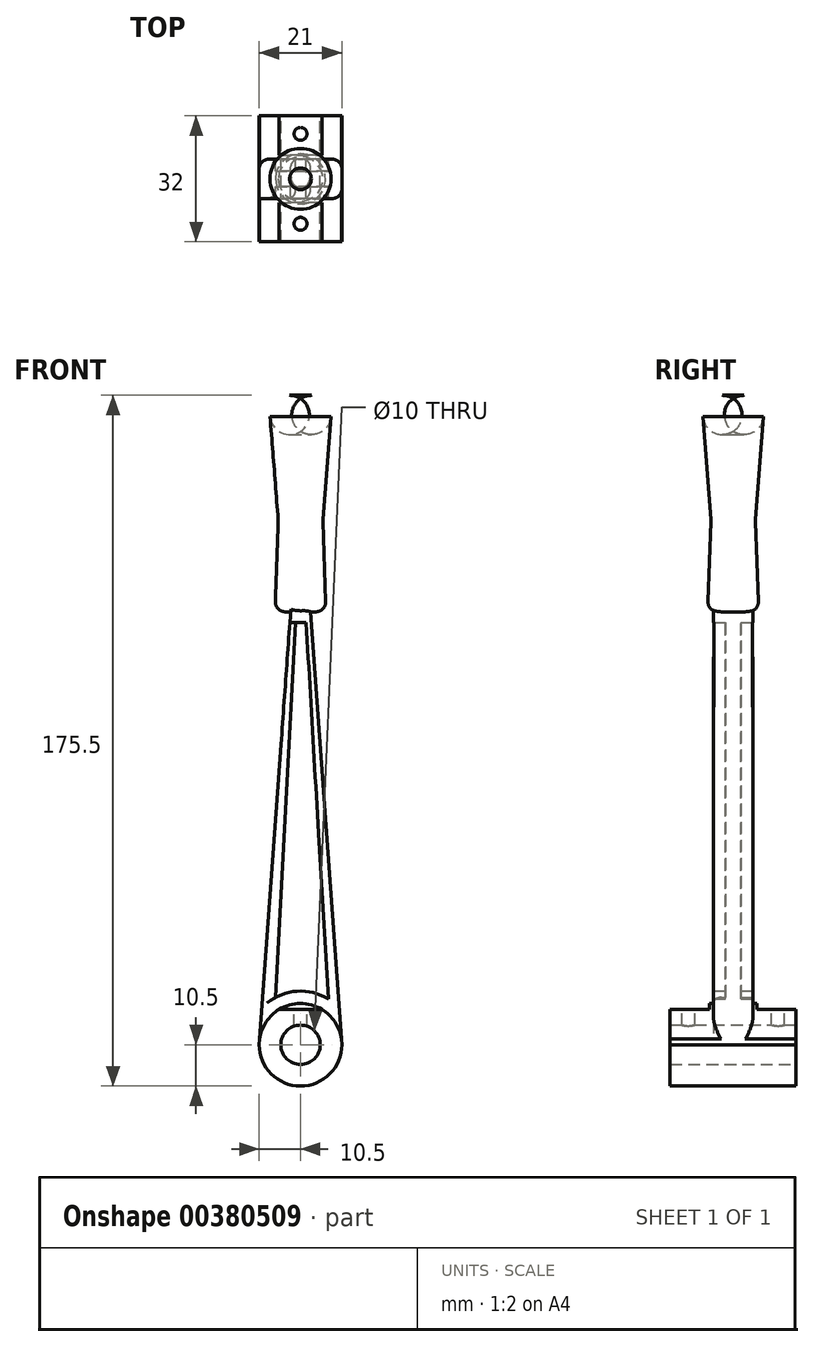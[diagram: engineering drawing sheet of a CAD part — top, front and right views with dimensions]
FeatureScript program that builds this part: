
annotation { "Feature Type Name" : "Feature", "Feature Type Description" : "" }
export const myFeature = defineFeature(function(context is Context, id is Id, definition is map)
    precondition{}
    {
        {
            var Q0;
            Q0=qCreatedBy(makeId("Front.planeOp"),FACE);
            var sketch = newSketch(context, id + "F0", { "sketchPlane" : qUnion([Q0])});
            skCircle(sketch, "E0", {"center": v(0, 0) * mm, "radius": 10.5 * mm});
            skCircle(sketch, "E1", {"center": v(0, 0) * mm, "radius": 5 * mm});
            skLineSegment(sketch, "E2", {"start": v(0, 0) * mm, "end": v(0, 110) * mm, "construction": true});
            skLineSegment(sketch, "E3", {"start": v(-10.5, 0) * mm, "end": v(10.5, 0) * mm, "construction": true});
            skLineSegment(sketch, "E4", {"start": v(2.5, 110) * mm, "end": v(-2.5, 110) * mm, "construction": true});
            skLineSegment(sketch, "E5", {"start": v(-10.5, 0) * mm, "end": v(-2.5, 110) * mm});
            skLineSegment(sketch, "E6", {"start": v(10.5, 0) * mm, "end": v(2.5, 110) * mm});
            skLineSegment(sketch, "E7", {"start": v(-2.5, 110) * mm, "end": v(-5.52, 110) * mm});
            skLineSegment(sketch, "E8", {"start": v(-5.52, 110) * mm, "end": v(-4.84, 133.19) * mm});
            skLineSegment(sketch, "E9", {"start": v(-4.84, 133.19) * mm, "end": v(-7.72, 159.46) * mm});
            skLineSegment(sketch, "E10", {"start": v(-2.75, 165) * mm, "end": v(2.75, 165) * mm});
            skLineSegment(sketch, "E11", {"start": v(7.73, 159.6) * mm, "end": v(5.68, 133.47) * mm});
            skLineSegment(sketch, "E12", {"start": v(5.67, 132.9) * mm, "end": v(6.48, 110) * mm});
            skLineSegment(sketch, "E13", {"start": v(6.48, 110) * mm, "end": v(2.5, 110) * mm});
            skPoint(sketch, "E14.visualSharp", {"position": v(-8.33, 165) * mm});
            skArc(sketch, "E14.filletArc", {"start": v(-2.75, 165) * mm, "mid": v(-6.47, 163.34) * mm, "end": v(-7.72, 159.46) * mm});
            skPoint(sketch, "E15.visualSharp", {"position": v(8.16, 165) * mm});
            skArc(sketch, "E15.filletArc", {"start": v(7.73, 159.6) * mm, "mid": v(6.42, 163.4) * mm, "end": v(2.75, 165) * mm});
            skLineSegment(sketch, "E16", {"start": v(-6.4, 12) * mm, "end": v(-1.29, 107.26) * mm});
            skLineSegment(sketch, "E17", {"start": v(1.44, 107.26) * mm, "end": v(7.06, 11.62) * mm});
            skArc(sketch, "E18", {"start": v(7.06, 11.62) * mm, "mid": v(0.38, 13.62) * mm, "end": v(-6.4, 12) * mm});
            skLineSegment(sketch, "E19", {"start": v(-1.29, 107.26) * mm, "end": v(1.44, 107.26) * mm});
            skLineSegment(sketch, "E20", {"start": v(0, 0) * mm, "end": v(0, 9) * mm});
            skLineSegment(sketch, "E21", {"start": v(-5.4, 9) * mm, "end": v(5.4, 9) * mm});
            skLineSegment(sketch, "E22", {"start": v(-2.5, 110) * mm, "end": v(2.5, 110) * mm});
            skPoint(sketch, "E23.visualSharp", {"position": v(5.66, 133.19) * mm});
            skArc(sketch, "E23.filletArc", {"start": v(5.68, 133.47) * mm, "mid": v(5.67, 133.19) * mm, "end": v(5.67, 132.9) * mm});
            skLineSegment(sketch, "E24", {"start": v(0, 165) * mm, "end": v(0, 110) * mm});
            skSolve(sketch);
        }
        {
            var Q0;
            Q0=makeQuery(id+"F0.imprint","IMPRINT",FACE,{"disambiguationData":[TD([[makeQuery(id+"F0.imprint","IMPRINT",EDGE,{"derivedFrom":sQuery(id+"F0.wireOp",EDGE,"E1")}),-1.0]])]});
            extrude(context, id + "F1", {"entities" : qUnion([Q0]), "depth" : 16 * mm, "hasSecondDirection" : true, "secondDirectionOppositeDirection" : true, "secondDirectionDepth" : 16 * mm});
        }
        {
            var Q0;
            Q0=makeQuery(id+"F0.imprint","IMPRINT",FACE,{"disambiguationData":[TD([[makeQuery(id+"F0.imprint","IMPRINT",EDGE,{"derivedFrom":sQuery(id+"F0.wireOp",EDGE,"E16")}),1.0]])]});
            extrude(context, id + "F2", {"entities" : qUnion([Q0]), "operationType" : NewBodyOperationType.ADD, "depth" : 5 * mm, "hasSecondDirection" : true, "secondDirectionOppositeDirection" : true, "secondDirectionDepth" : 5 * mm});
        }
        {
            var Q0;
            Q0=makeQuery(id+"F0.imprint","IMPRINT",FACE,{"disambiguationData":[TD([[makeQuery(id+"F0.imprint","IMPRINT",EDGE,{"derivedFrom":sQuery(id+"F0.wireOp",EDGE,"E11")}),-1.0]])]});
            var Q1;
            Q1=sQuery(id+"F0.wireOp",EDGE,"E2");
            revolve(context, id + "F3", {"operationType" : NewBodyOperationType.ADD, "entities" : qUnion([Q0]), "axis" : qUnion([Q1]), "revolveType" : RevolveType.FULL});
        }
        {
            var Q0;
            Q0=makeQuery(id+"F3.opRevolve","SWEPT_EDGE",EDGE,{"disambiguationData":[OSD([sQuery(id+"F0.wireOp",EDGE,"E12"),sQuery(id+"F0.wireOp",EDGE,"E13")])]});
            fillet(context, id + "F4", {"entities" : qUnion([Q0]), "radius" : 2.5 * mm, "tangentPropagation" : true, "allowEdgeOverflow" : false});
        }
        {
            var Q0;
            {var subQ0=sQuery(id+"F0.wireOp",EDGE,"E21");var subQ4=makeQuery(id+"F0.imprint","IMPRINT",VERTEX,{"derivedFrom":subQ0});Q0=makeQuery(id+"F0.imprint","IMPRINT",FACE,{"disambiguationData":[TD([[makeQuery(id+"F0.imprint","IMPRINT",EDGE,{"disambiguationData":[TD([[subQ4,1.0]])],"derivedFrom":subQ0}),1.0]])]});}
            extrude(context, id + "F5", {"entities" : qUnion([Q0]), "operationType" : NewBodyOperationType.ADD, "oppositeDirection" : true, "depth" : 6 * mm, "hasSecondDirection" : true, "secondDirectionOppositeDirection" : false, "secondDirectionDepth" : 6 * mm});
        }
        {
            var Q0;
            {var subQ0=sQuery(id+"F0.wireOp",EDGE,"E0");var subQ1=sQuery(id+"F0.wireOp",EDGE,"E21");Q0=makeQuery(id+"F5.boolean.opBoolean","SPLIT",FACE,{"disambiguationData":[TD([makeQuery(id+"F5.opExtrude","CAP_FACE",FACE,{"disambiguationData":[OSD([subQ0,subQ1])],"isStart":false})])],"derivedFrom":makeQuery(id+"F1.opExtrude","SWEPT_FACE",FACE,{"disambiguationData":[OSD([subQ1])]})});}
            var sketch = newSketch(context, id + "F6", { "sketchPlane" : qUnion([Q0])});
            skCircle(sketch, "E25", {"center": v(0, 11.42) * mm, "radius": 2.1 * mm});
            skPoint(sketch, "E25.centerSnap0", {"position": v(0, 6) * mm});
            skCircle(sketch, "E26.MirrorC", {"center": v(0, -11.42) * mm, "radius": 2.1 * mm});
            skSolve(sketch);
        }
        {
            var Q0;
            Q0=sQuery(id+"F6.wireOp",VERTEX,"E25.center");
            var Q1;
            Q1=sQuery(id+"F6.wireOp",VERTEX,"E26.MirrorC.center");
            var Q2;
            Q2=makeQuery(id+"F1.opExtrude","SWEPT_BODY",BODY,{"disambiguationData":[OSD([sQuery(id+"F0.wireOp",EDGE,"E0"),sQuery(id+"F0.wireOp",EDGE,"E1"),sQuery(id+"F0.wireOp",EDGE,"E5"),sQuery(id+"F0.wireOp",EDGE,"E6"),sQuery(id+"F0.wireOp",EDGE,"E21")])]});
            hole(context, id + "F7", {"style" : HoleStyle.SIMPLE, "endStyle" : HoleEndStyle.BLIND, "holeDiameter" : 3.3 * mm, "holeDepth" : 6 * mm, "isTappedThrough" : true, "tappedDepth" : 12.7 * mm, "tapClearance" : 3, "locations" : qUnion([Q0, Q1]), "scope" : qUnion([Q2])});
        }
        {
            var Q0;
            Q0=makeQuery(id+"F0.imprint","IMPRINT",FACE,{"disambiguationData":[TD([[makeQuery(id+"F0.imprint","IMPRINT",EDGE,{"derivedFrom":sQuery(id+"F0.wireOp",EDGE,"E16")}),-1.0]])]});
            extrude(context, id + "F8", {"entities" : qUnion([Q0]), "operationType" : NewBodyOperationType.ADD, "oppositeDirection" : true, "depth" : 2 * mm, "hasSecondDirection" : true, "secondDirectionOppositeDirection" : false, "secondDirectionDepth" : 2 * mm});
        }
        {
            var Q0;
            Q0=makeQuery(id+"F2.opExtrude","CAP_EDGE",EDGE,{"disambiguationData":[OSD([sQuery(id+"F0.wireOp",EDGE,"E5")])],"isStart":true});
            var Q1;
            Q1=makeQuery(id+"F2.opExtrude","CAP_EDGE",EDGE,{"disambiguationData":[OSD([sQuery(id+"F0.wireOp",EDGE,"E16")])],"isStart":false});
            var Q2;
            Q2=makeQuery(id+"F2.opExtrude","CAP_EDGE",EDGE,{"disambiguationData":[OSD([sQuery(id+"F0.wireOp",EDGE,"E6")])],"isStart":false});
            var Q3;
            Q3=makeQuery(id+"F2.opExtrude","CAP_EDGE",EDGE,{"disambiguationData":[OSD([sQuery(id+"F0.wireOp",EDGE,"E6")])],"isStart":true});
            fillet(context, id + "F9", {"entities" : qUnion([Q0, Q1, Q2, Q3]), "radius" : 2 * mm, "tangentPropagation" : true, "allowEdgeOverflow" : false});
        }
    });
